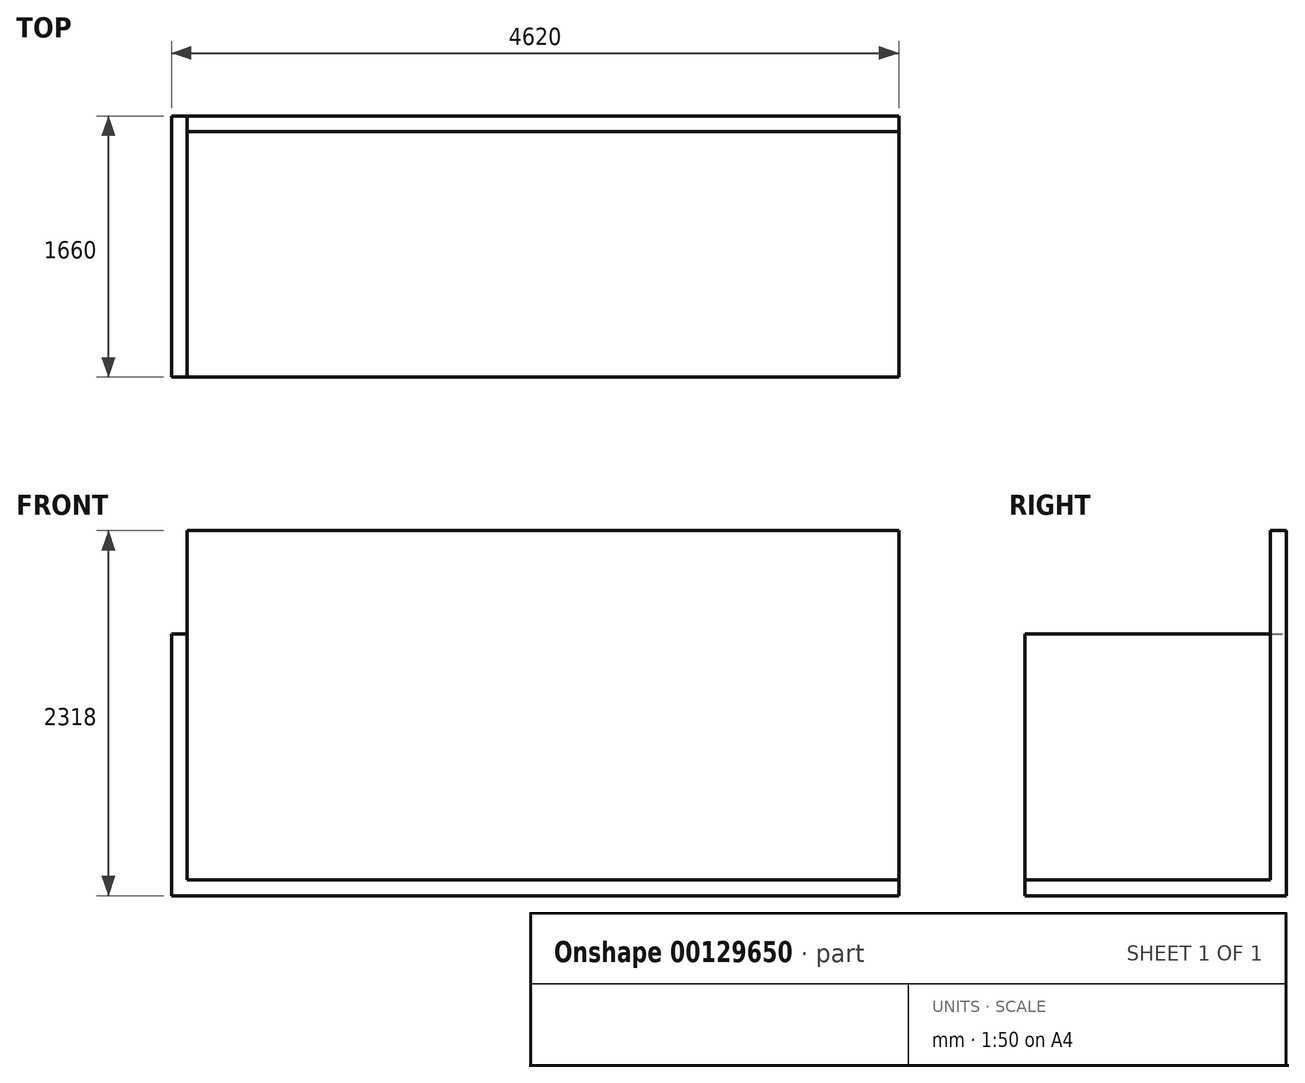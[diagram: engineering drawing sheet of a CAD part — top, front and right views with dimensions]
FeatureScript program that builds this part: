
annotation { "Feature Type Name" : "Feature", "Feature Type Description" : "" }
export const myFeature = defineFeature(function(context is Context, id is Id, definition is map)
    precondition{}
    {
        {
            var Q0;
            Q0=qCreatedBy(makeId("Top.planeOp"),FACE);
            var sketch = newSketch(context, id + "F0", { "sketchPlane" : qUnion([Q0])});
            skLineSegment(sketch, "E0.bottom", {"start": v(-4520, 0) * mm, "end": v(0, 0) * mm});
            skLineSegment(sketch, "E0.top", {"start": v(-4520, 1560) * mm, "end": v(0, 1560) * mm});
            skLineSegment(sketch, "E0.left", {"start": v(-4520, 0) * mm, "end": v(-4520, 1560) * mm});
            skLineSegment(sketch, "E0.right", {"start": v(0, 0) * mm, "end": v(0, 1560) * mm});
            skLineSegment(sketch, "E1", {"start": v(0, 1560) * mm, "end": v(0, 1660) * mm});
            skLineSegment(sketch, "E2", {"start": v(0, 1660) * mm, "end": v(-4520, 1660) * mm});
            skLineSegment(sketch, "E3", {"start": v(-4520, 1660) * mm, "end": v(-4520, 1560) * mm});
            skLineSegment(sketch, "E4", {"start": v(-4520, 1660) * mm, "end": v(-4620, 1660) * mm});
            skLineSegment(sketch, "E5", {"start": v(-4620, 1660) * mm, "end": v(-4620, 0) * mm});
            skLineSegment(sketch, "E6", {"start": v(-4620, 0) * mm, "end": v(-4520, 0) * mm});
            skSolve(sketch);
        }
        {
            var Q0;
            Q0=makeQuery(id+"F0.imprint","IMPRINT",FACE,{"disambiguationData":[TD([[makeQuery(id+"F0.imprint","IMPRINT",EDGE,{"derivedFrom":sQuery(id+"F0.wireOp",EDGE,"E0.bottom")}),1.0]])]});
            extrude(context, id + "F1", {"entities" : qUnion([Q0]), "oppositeDirection" : true, "depth" : 100 * mm});
        }
        {
            var Q0;
            Q0=makeQuery(id+"F0.imprint","IMPRINT",FACE,{"disambiguationData":[TD([[makeQuery(id+"F0.imprint","IMPRINT",EDGE,{"derivedFrom":sQuery(id+"F0.wireOp",EDGE,"E0.top")}),1.0]])]});
            extrude(context, id + "F2", {"entities" : qUnion([Q0]), "depth" : 2218 * mm});
        }
        {
            var Q0;
            Q0=makeQuery(id+"F0.imprint","IMPRINT",FACE,{"disambiguationData":[TD([[makeQuery(id+"F0.imprint","IMPRINT",EDGE,{"derivedFrom":sQuery(id+"F0.wireOp",EDGE,"E0.top")}),1.0]])]});
            extrude(context, id + "F3", {"entities" : qUnion([Q0]), "operationType" : NewBodyOperationType.ADD, "oppositeDirection" : true, "depth" : 100 * mm});
        }
        {
            var Q0;
            Q0=makeQuery(id+"F0.imprint","IMPRINT",FACE,{"disambiguationData":[TD([[makeQuery(id+"F0.imprint","IMPRINT",EDGE,{"derivedFrom":sQuery(id+"F0.wireOp",EDGE,"E0.left")}),1.0]])]});
            extrude(context, id + "F4", {"entities" : qUnion([Q0]), "depth" : 1561 * mm});
        }
        {
            var Q0;
            Q0=makeQuery(id+"F0.imprint","IMPRINT",FACE,{"disambiguationData":[TD([[makeQuery(id+"F0.imprint","IMPRINT",EDGE,{"derivedFrom":sQuery(id+"F0.wireOp",EDGE,"E0.left")}),1.0]])]});
            extrude(context, id + "F5", {"entities" : qUnion([Q0]), "operationType" : NewBodyOperationType.ADD, "oppositeDirection" : true, "depth" : 100 * mm});
        }
    });
